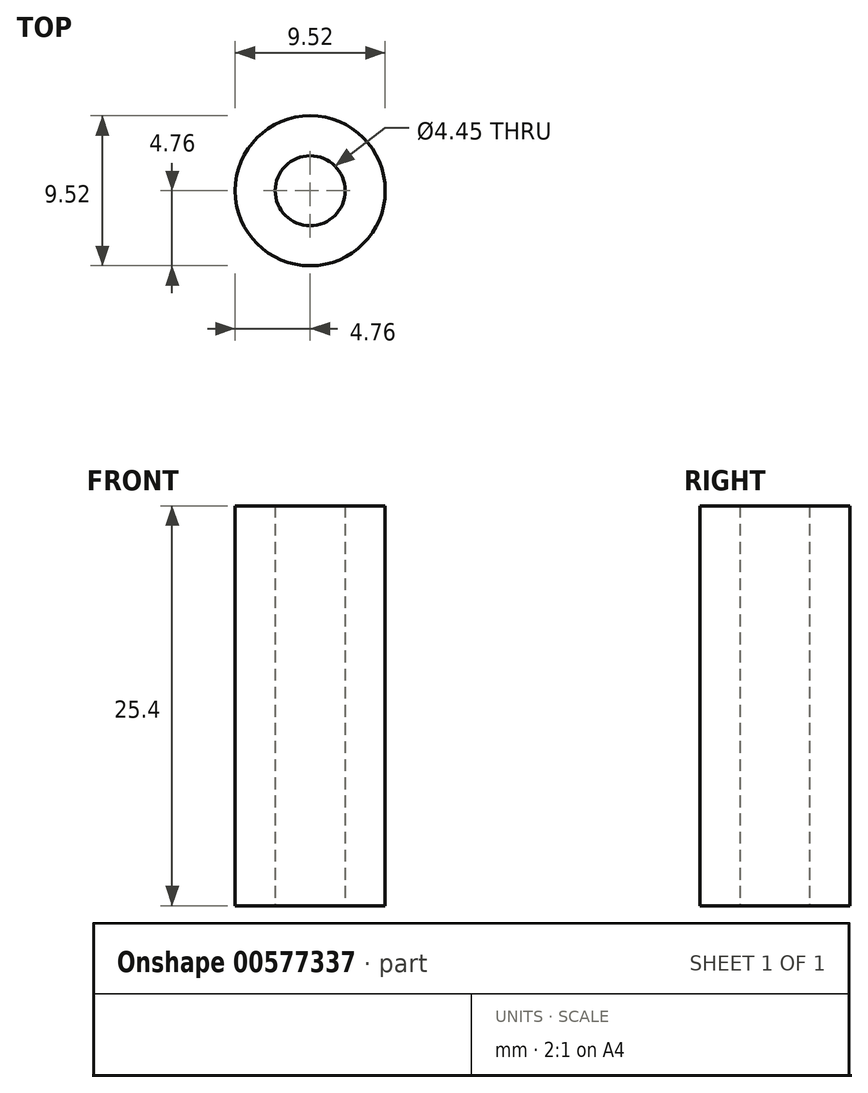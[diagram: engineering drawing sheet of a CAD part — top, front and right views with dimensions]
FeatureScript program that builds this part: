
annotation { "Feature Type Name" : "Feature", "Feature Type Description" : "" }
export const myFeature = defineFeature(function(context is Context, id is Id, definition is map)
    precondition{}
    {
        {
            var Q0;
            Q0=qCreatedBy(makeId("Top.planeOp"),FACE);
            var sketch = newSketch(context, id + "F0", { "sketchPlane" : qUnion([Q0])});
            skCircle(sketch, "E0", {"center": v(0, 0) * mm, "radius": 2.22 * mm});
            skCircle(sketch, "E1", {"center": v(0, 0) * mm, "radius": 4.76 * mm});
            skSolve(sketch);
        }
        {
            var Q0;
            Q0 = qSketchRegion(id + "F0", true);
            extrude(context, id + "F1", {"entities" : qUnion([Q0]), "endBound" : BoundingType.SYMMETRIC, "depth" : 25.4 * mm, "offsetDistance" : 25.4 * mm});
        }
    });
